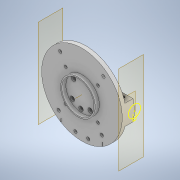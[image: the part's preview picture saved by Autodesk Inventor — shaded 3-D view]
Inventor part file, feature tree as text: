
AUTODESK INVENTOR PART (.ipt)
format: ipt  version: 2021 (Build 250183000, 183)  size: 412,160 bytes
history: native  units: mm
features: reference x30, other x19, sketch x16, extrude x14, direct_edit x14, move_body x5, plane x3, mirror x2, projected_geometry x1
ambient origin geometry x8: Origin, YZ Plane, XZ Plane, XY Plane, X Axis, Y Axis, Z Axis, Center Point
bodies: Solid1 (feature_tree)
feature tree (104):
  extrude  "Extrusion1"  Depth=5.0mm TaperAngle=0.0deg
  extrude  "Extrusion2"  Depth=43.0mm
  extrude  "Extrusion3"  Depth=3.0mm TaperAngle=0.0deg
  extrude  "Extrusion4"  Depth=10.0mm TaperAngle=0.0deg
  extrude  "Extrusion5"  Depth=5.0mm
  extrude  "Extrusion6"  Depth=3.2mm
  plane  "Work Plane1"
  plane  "Work Plane2"
  sketch  "Sketch10"  dims[d29=28.0mm d30=0.0mm d31=10.0mm d32=0.0mm]
  sketch  "Sketch11"  dims[d33=2.0mm d49=0.0mm d50=0.0mm]
  plane  "Work Plane3"
  extrude  "Extrusion10"  Depth=28.0mm TaperAngle=0.0deg
  extrude  "Extrusion11"  Depth=10.0mm TaperAngle=0.0deg
  mirror  "Mirror3"
  extrude  "Extrusion12"  TaperAngle=0.0deg  [1 undecoded]
  extrude  "Extrusion13"  Depth=5.0mm
  extrude  "Extrusion14"  [1 undecoded]
  direct_edit  "Direct Edit1"
  extrude  "Extrusion15"  Depth=33.0mm
  direct_edit  "Direct Edit2"
  extrude  "Extrusion16"  Depth=4.0mm
  direct_edit  "Direct Edit3"
  extrude  "Extrusion17"  [1 undecoded]
  direct_edit  "Direct Edit4"
  direct_edit  "Direct Edit5"
  direct_edit  "Direct Edit6"
  direct_edit  "Direct Edit7"
  direct_edit  "Direct Edit8"
  mirror  "Mirror4"
  direct_edit  "Direct Edit9"
  direct_edit  "Direct Edit10"
  direct_edit  "Direct Edit11"
  direct_edit  "Direct Edit12"
  direct_edit  "Direct Edit13"
  direct_edit  "Direct Edit14"
  sketch  "Sketch1"  dims[d0=10.0mm d1=0.0mm d2=5.0mm d3=0.0mm]
  reference  "Reference1"
  sketch  "Sketch2"  dims[d4=17.25mm d5=0.0mm d6=43.0mm]
  reference  "Reference2"
  reference  "Reference3"
  sketch  "Sketch3"  dims[d7=40.0mm d8=3.0mm d9=0.0mm]
  reference  "Reference4"
  reference  "Reference5"
  reference  "Reference6"
  reference  "Reference7"
  reference  "Reference8"
  reference  "Reference9"
  reference  "Reference10"
  reference  "Reference11"
  sketch  "Sketch4"  dims[d10=10.0mm d11=0.0mm d12=10.0mm d13=0.0mm]
  reference  "Reference12"
  sketch  "Sketch6"  dims[d20=5.0mm d21=0.0mm d22=5.0mm]
  reference  "Reference15"
  reference  "Reference16"
  sketch  "Sketch7"  dims[d23=8.0mm d24=3.2mm]
  projected_geometry  "Projected Loop1"
  sketch  "Sketch9"  dims[d25=0.0mm d26=0.0mm d27=28.0mm d28=0.0mm]
  reference  "Reference27"
  reference  "Reference28"
  reference  "Reference29"
  reference  "Reference30"
  reference  "Reference31"
  reference  "Reference32"
  reference  "Reference33"
  reference  "Reference34"
  sketch  "Sketch13"  dims[d51=5.0mm d52=5.0mm]
  sketch  "Sketch14"  dims[d53=2.0mm d54=0.0mm d55=-2.0mm]
  sketch  "Sketch15"  dims[d56=85.0mm d57=33.0mm]
  reference  "Reference35"
  reference  "Reference36"
  reference  "Reference37"
  reference  "Reference38"
  reference  "Reference39"
  reference  "Reference40"
  reference  "Reference41"
  reference  "Reference42"
  sketch  "Sketch16"  dims[d58=4.0mm d59=4.0mm]
  sketch  "Sketch17"  dims[d60=0.0mm d61=0.0mm d62=-0.5mm]
  sketch  "Sketch18"  dims[d63=0.0mm d64=-1.5mm d65=0.0mm]
  sketch  "Sketch19"  dims[d66=0.0mm d67=-1.0mm d68=0.0mm d69=-0.5mm d70=-0.25mm d71=-2.0mm d72=-2.0mm d73=0.0mm d74=0.0mm d75=0.0mm d76=-2.25mm d77=0.0mm d78=0.0mm d79=-2.0mm d80=-0.5mm d81=2.0mm d82=-2.0mm d83=-2.0mm d16=0.5mm d17=0.872665mm d18=0.5mm d19=0.872665mm]
  parser-record x2  (decoder bookkeeping rows leaked as tree rows — omitted from the tree; the rows remain in map.json)
  other  "whole_assembly.iam"
  other  "tool_holder:1"
  other  "robot_with_gripper.iam"
  other  "IRB120_3-58_IRC5_rev1:1"
  other  "IRB120_3-58_IRC5_Link6_rev1_6"
  other  "539636 HGP-16-A-B-SSK---(asm_0_-ZH):1"
  other  "gripper extension:1"
  other  "Size1"
  other  "Delete1"
  other  "Size2"
  other  "Size3"
  move_body  "Move1"
  move_body  "Move2"
  other  "Size4"
  other  "Size5"
  move_body  "Move3"
  move_body  "Move4"
  move_body  "Move5"
  other  "Size6"
  other  "Size7"
  other  "Size8"
  other  "Size9"
note: 3 required parameter values undecoded (feature->parameter linkage not recoverable at this tier; creation-order binding heuristic only, values carry confidence <= 0.55)
note: 2 file-system paths scrubbed to <path> (originals preserved in map.json)
